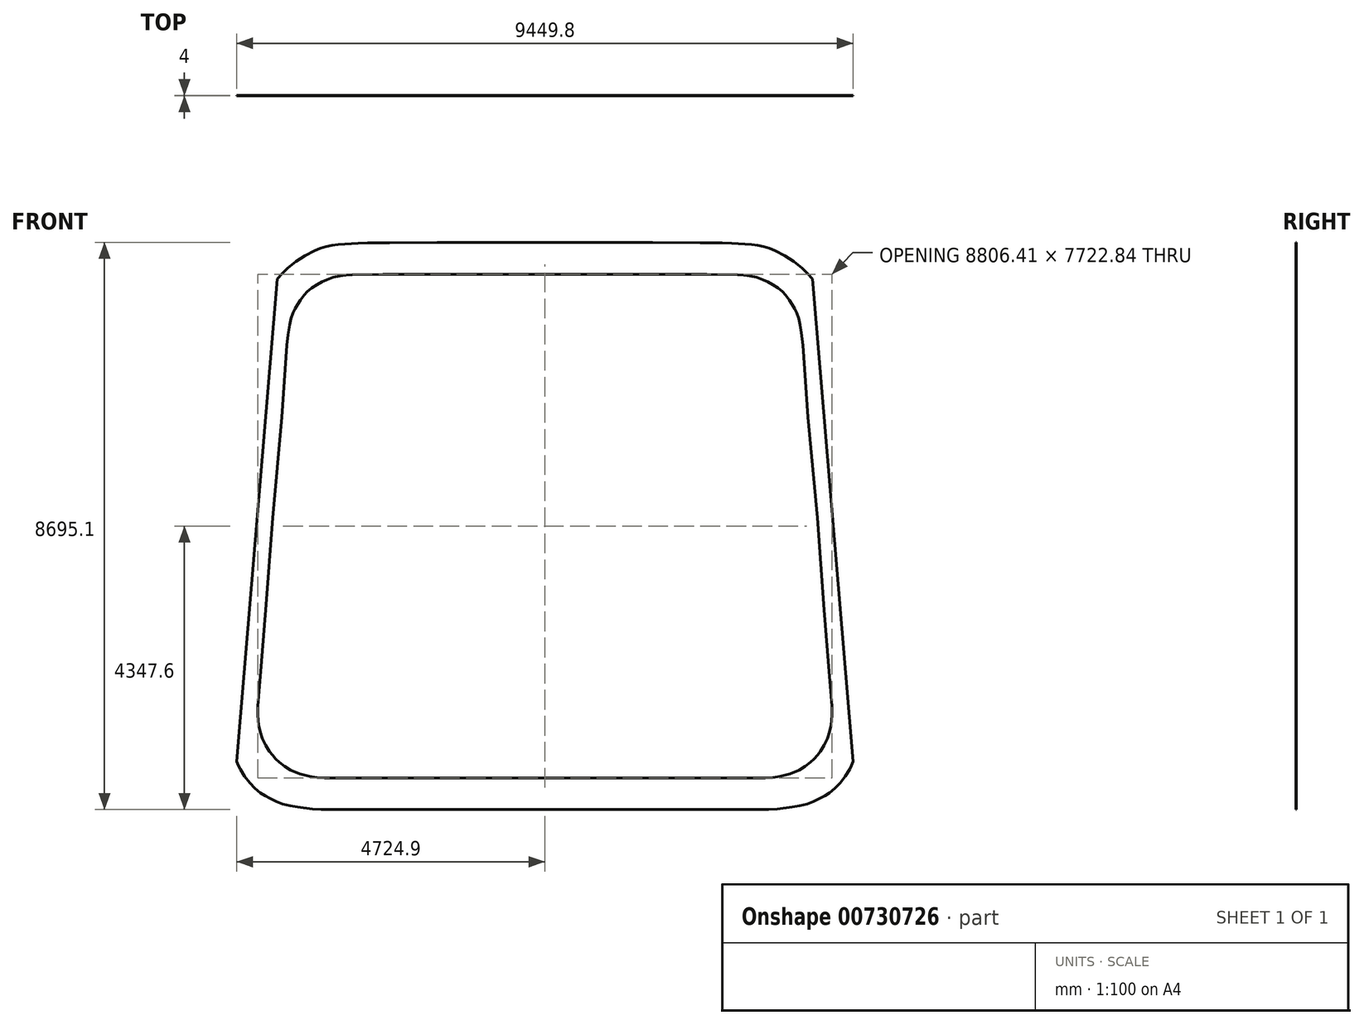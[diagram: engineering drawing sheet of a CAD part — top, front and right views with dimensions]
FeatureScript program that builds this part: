
annotation { "Feature Type Name" : "Feature", "Feature Type Description" : "" }
export const myFeature = defineFeature(function(context is Context, id is Id, definition is map)
    precondition{}
    {
        {
            var Q0;
            Q0=qCreatedBy(makeId("Front.planeOp"),FACE);
            var sketch = newSketch(context, id + "F0", { "sketchPlane" : qUnion([Q0])});
            skLineSegment(sketch, "E0", {"start": v(-4100.23, 3791.6) * mm, "end": v(-3973.7, 3780.9) * mm});
            skLineSegment(sketch, "E1", {"start": v(-3973.7, 3780.9) * mm, "end": v(-4100.23, 3791.6) * mm});
            skLineSegment(sketch, "E2", {"start": v(-4100.23, 3791.6) * mm, "end": v(-4023.75, 3874.4) * mm});
            skLineSegment(sketch, "E3", {"start": v(-4023.75, 3874.4) * mm, "end": v(-3941.84, 3951.8) * mm});
            skLineSegment(sketch, "E4", {"start": v(-3941.84, 3951.8) * mm, "end": v(-3814.61, 4053.62) * mm});
            skLineSegment(sketch, "E5", {"start": v(-3814.61, 4053.62) * mm, "end": v(-3675.57, 4146.44) * mm});
            skLineSegment(sketch, "E6", {"start": v(-3675.57, 4146.44) * mm, "end": v(-3530.84, 4221.57) * mm});
            skLineSegment(sketch, "E7", {"start": v(-3530.84, 4221.57) * mm, "end": v(-3443.72, 4257.71) * mm});
            skLineSegment(sketch, "E8", {"start": v(-3443.72, 4257.71) * mm, "end": v(-3354, 4285.83) * mm});
            skLineSegment(sketch, "E9", {"start": v(-3354, 4285.83) * mm, "end": v(-3261.07, 4304.07) * mm});
            skLineSegment(sketch, "E10", {"start": v(-3261.07, 4304.07) * mm, "end": v(-3166.73, 4315.7) * mm});
            skLineSegment(sketch, "E11", {"start": v(-3166.73, 4315.7) * mm, "end": v(-2864.57, 4338.46) * mm});
            skLineSegment(sketch, "E12", {"start": v(-2864.57, 4338.46) * mm, "end": v(-2717.79, 4342.65) * mm});
            skLineSegment(sketch, "E13", {"start": v(-2717.79, 4342.65) * mm, "end": v(-2714.16, 4215.7) * mm});
            skLineSegment(sketch, "E14", {"start": v(-2714.16, 4215.7) * mm, "end": v(-2717.79, 4342.65) * mm});
            skLineSegment(sketch, "E15", {"start": v(-2717.79, 4342.65) * mm, "end": v(-2379.79, 4343.31) * mm});
            skLineSegment(sketch, "E16", {"start": v(-2379.79, 4343.31) * mm, "end": v(-1650.99, 4346.03) * mm});
            skLineSegment(sketch, "E17", {"start": v(-1650.99, 4346.03) * mm, "end": v(-1312.13, 4347.55) * mm});
            skLineSegment(sketch, "E18", {"start": v(-1312.13, 4347.55) * mm, "end": v(-177.03, 4347.55) * mm});
            skLineSegment(sketch, "E19", {"start": v(-177.03, 4347.55) * mm, "end": v(-0.01, 4347.55) * mm});
            skLineSegment(sketch, "E20", {"start": v(-0.01, 4347.55) * mm, "end": v(-0.01, 4220.55) * mm});
            skLineSegment(sketch, "E21", {"start": v(-0.01, 4220.55) * mm, "end": v(-0.01, 4347.55) * mm});
            skLineSegment(sketch, "E22", {"start": v(-0.01, 4347.55) * mm, "end": v(177, 4347.55) * mm});
            skLineSegment(sketch, "E23", {"start": v(177, 4347.55) * mm, "end": v(1312.13, 4347.55) * mm});
            skLineSegment(sketch, "E24", {"start": v(1312.13, 4347.55) * mm, "end": v(1650.99, 4346.03) * mm});
            skLineSegment(sketch, "E25", {"start": v(1650.99, 4346.03) * mm, "end": v(2379.79, 4343.31) * mm});
            skLineSegment(sketch, "E26", {"start": v(2379.79, 4343.31) * mm, "end": v(2717.79, 4342.65) * mm});
            skLineSegment(sketch, "E27", {"start": v(2717.79, 4342.65) * mm, "end": v(2717.53, 4215.65) * mm});
            skLineSegment(sketch, "E28", {"start": v(2717.53, 4215.65) * mm, "end": v(2717.79, 4342.65) * mm});
            skLineSegment(sketch, "E29", {"start": v(2717.79, 4342.65) * mm, "end": v(2864.57, 4338.46) * mm});
            skLineSegment(sketch, "E30", {"start": v(2864.57, 4338.46) * mm, "end": v(3166.73, 4315.7) * mm});
            skLineSegment(sketch, "E31", {"start": v(3166.73, 4315.7) * mm, "end": v(3261.04, 4304.07) * mm});
            skLineSegment(sketch, "E32", {"start": v(3261.04, 4304.07) * mm, "end": v(3354, 4285.83) * mm});
            skLineSegment(sketch, "E33", {"start": v(3354, 4285.83) * mm, "end": v(3443.72, 4257.71) * mm});
            skLineSegment(sketch, "E34", {"start": v(3443.72, 4257.71) * mm, "end": v(3530.84, 4221.57) * mm});
            skLineSegment(sketch, "E35", {"start": v(3530.84, 4221.57) * mm, "end": v(3675.57, 4146.44) * mm});
            skLineSegment(sketch, "E36", {"start": v(3675.57, 4146.44) * mm, "end": v(3814.61, 4053.62) * mm});
            skLineSegment(sketch, "E37", {"start": v(3814.61, 4053.62) * mm, "end": v(3941.81, 3951.8) * mm});
            skLineSegment(sketch, "E38", {"start": v(3941.81, 3951.8) * mm, "end": v(4023.75, 3874.4) * mm});
            skLineSegment(sketch, "E39", {"start": v(4023.75, 3874.4) * mm, "end": v(4100.23, 3791.6) * mm});
            skLineSegment(sketch, "E40", {"start": v(4100.23, 3791.6) * mm, "end": v(4006.94, 3705.42) * mm});
            skLineSegment(sketch, "E41", {"start": v(4006.94, 3705.42) * mm, "end": v(4100.23, 3791.6) * mm});
            skLineSegment(sketch, "E42", {"start": v(4100.23, 3791.6) * mm, "end": v(4724.9, -3609.56) * mm});
            skLineSegment(sketch, "E43", {"start": v(4724.9, -3609.56) * mm, "end": v(4598.35, -3620.22) * mm});
            skLineSegment(sketch, "E44", {"start": v(4598.35, -3620.22) * mm, "end": v(4724.9, -3609.56) * mm});
            skLineSegment(sketch, "E45", {"start": v(4724.9, -3609.56) * mm, "end": v(4697.95, -3673.59) * mm});
            skLineSegment(sketch, "E46", {"start": v(4697.95, -3673.59) * mm, "end": v(4670.34, -3731.88) * mm});
            skLineSegment(sketch, "E47", {"start": v(4670.34, -3731.88) * mm, "end": v(4605.29, -3835.34) * mm});
            skLineSegment(sketch, "E48", {"start": v(4605.29, -3835.34) * mm, "end": v(4524.26, -3938.16) * mm});
            skLineSegment(sketch, "E49", {"start": v(4524.26, -3938.16) * mm, "end": v(4447.4, -4018.22) * mm});
            skLineSegment(sketch, "E50", {"start": v(4447.4, -4018.22) * mm, "end": v(4362, -4088.6) * mm});
            skLineSegment(sketch, "E51", {"start": v(4362, -4088.6) * mm, "end": v(4289.7, -4135) * mm});
            skLineSegment(sketch, "E52", {"start": v(4289.7, -4135) * mm, "end": v(4214.05, -4176.59) * mm});
            skLineSegment(sketch, "E53", {"start": v(4214.05, -4176.59) * mm, "end": v(4117.45, -4224.67) * mm});
            skLineSegment(sketch, "E54", {"start": v(4117.45, -4224.67) * mm, "end": v(4017.58, -4263.7) * mm});
            skLineSegment(sketch, "E55", {"start": v(4017.58, -4263.7) * mm, "end": v(3904.88, -4290.91) * mm});
            skLineSegment(sketch, "E56", {"start": v(3904.88, -4290.91) * mm, "end": v(3789.7, -4309.43) * mm});
            skLineSegment(sketch, "E57", {"start": v(3789.7, -4309.43) * mm, "end": v(3564.62, -4339.93) * mm});
            skLineSegment(sketch, "E58", {"start": v(3564.62, -4339.93) * mm, "end": v(3428.99, -4347.55) * mm});
            skLineSegment(sketch, "E59", {"start": v(3428.99, -4347.55) * mm, "end": v(3421.88, -4220.73) * mm});
            skLineSegment(sketch, "E60", {"start": v(3421.88, -4220.73) * mm, "end": v(3428.99, -4347.55) * mm});
            skLineSegment(sketch, "E61", {"start": v(3428.99, -4347.55) * mm, "end": v(3169.86, -4347.55) * mm});
            skLineSegment(sketch, "E62", {"start": v(3169.86, -4347.55) * mm, "end": v(2285.99, -4347.55) * mm});
            skLineSegment(sketch, "E63", {"start": v(2285.99, -4347.55) * mm, "end": v(2195.92, -4347.55) * mm});
            skLineSegment(sketch, "E64", {"start": v(2195.92, -4347.55) * mm, "end": v(1142.99, -4347.55) * mm});
            skLineSegment(sketch, "E65", {"start": v(1142.99, -4347.55) * mm, "end": v(1138.31, -4347.55) * mm});
            skLineSegment(sketch, "E66", {"start": v(1138.31, -4347.55) * mm, "end": v(-0.01, -4347.55) * mm});
            skLineSegment(sketch, "E67", {"start": v(-0.01, -4347.55) * mm, "end": v(-0.01, -4220.55) * mm});
            skLineSegment(sketch, "E68", {"start": v(-0.01, -4220.55) * mm, "end": v(-0.01, -4347.55) * mm});
            skLineSegment(sketch, "E69", {"start": v(-0.01, -4347.55) * mm, "end": v(-1138.31, -4347.55) * mm});
            skLineSegment(sketch, "E70", {"start": v(-1138.31, -4347.55) * mm, "end": v(-1143.01, -4347.55) * mm});
            skLineSegment(sketch, "E71", {"start": v(-1143.01, -4347.55) * mm, "end": v(-2195.92, -4347.55) * mm});
            skLineSegment(sketch, "E72", {"start": v(-2195.92, -4347.55) * mm, "end": v(-2286.01, -4347.55) * mm});
            skLineSegment(sketch, "E73", {"start": v(-2286.01, -4347.55) * mm, "end": v(-3169.86, -4347.55) * mm});
            skLineSegment(sketch, "E74", {"start": v(-3169.86, -4347.55) * mm, "end": v(-3429.01, -4347.55) * mm});
            skLineSegment(sketch, "E75", {"start": v(-3429.01, -4347.55) * mm, "end": v(-3429.01, -4220.55) * mm});
            skLineSegment(sketch, "E76", {"start": v(-3429.01, -4220.55) * mm, "end": v(-3429.01, -4347.55) * mm});
            skLineSegment(sketch, "E77", {"start": v(-3429.01, -4347.55) * mm, "end": v(-3564.62, -4339.93) * mm});
            skLineSegment(sketch, "E78", {"start": v(-3564.62, -4339.93) * mm, "end": v(-3789.7, -4309.43) * mm});
            skLineSegment(sketch, "E79", {"start": v(-3789.7, -4309.43) * mm, "end": v(-3904.88, -4290.91) * mm});
            skLineSegment(sketch, "E80", {"start": v(-3904.88, -4290.91) * mm, "end": v(-4017.58, -4263.7) * mm});
            skLineSegment(sketch, "E81", {"start": v(-4017.58, -4263.7) * mm, "end": v(-4117.45, -4224.67) * mm});
            skLineSegment(sketch, "E82", {"start": v(-4117.45, -4224.67) * mm, "end": v(-4214.05, -4176.59) * mm});
            skLineSegment(sketch, "E83", {"start": v(-4214.05, -4176.59) * mm, "end": v(-4289.7, -4135) * mm});
            skLineSegment(sketch, "E84", {"start": v(-4289.7, -4135) * mm, "end": v(-4362, -4088.6) * mm});
            skLineSegment(sketch, "E85", {"start": v(-4362, -4088.6) * mm, "end": v(-4447.4, -4018.22) * mm});
            skLineSegment(sketch, "E86", {"start": v(-4447.4, -4018.22) * mm, "end": v(-4524.26, -3938.16) * mm});
            skLineSegment(sketch, "E87", {"start": v(-4524.26, -3938.16) * mm, "end": v(-4605.29, -3835.34) * mm});
            skLineSegment(sketch, "E88", {"start": v(-4605.29, -3835.34) * mm, "end": v(-4670.34, -3731.88) * mm});
            skLineSegment(sketch, "E89", {"start": v(-4670.34, -3731.88) * mm, "end": v(-4697.95, -3673.59) * mm});
            skLineSegment(sketch, "E90", {"start": v(-4697.95, -3673.59) * mm, "end": v(-4724.9, -3609.56) * mm});
            skLineSegment(sketch, "E91", {"start": v(-4724.9, -3609.56) * mm, "end": v(-4607.85, -3560.28) * mm});
            skLineSegment(sketch, "E92", {"start": v(-4607.85, -3560.28) * mm, "end": v(-4724.9, -3609.56) * mm});
            skLineSegment(sketch, "E93", {"start": v(-4724.9, -3609.56) * mm, "end": v(-4100.23, 3791.6) * mm});
            skLineSegment(sketch, "E94", {"start": v(1492.57, 3861.47) * mm, "end": v(-0.01, 3861.47) * mm});
            skLineSegment(sketch, "E95", {"start": v(-0.01, 3861.47) * mm, "end": v(-0.01, 3988.47) * mm});
            skLineSegment(sketch, "E96", {"start": v(-0.01, 3988.47) * mm, "end": v(-0.01, 3861.47) * mm});
            skLineSegment(sketch, "E97", {"start": v(-0.01, 3861.47) * mm, "end": v(-1492.6, 3861.47) * mm});
            skLineSegment(sketch, "E98", {"start": v(-1492.6, 3861.47) * mm, "end": v(-2485.66, 3861.47) * mm});
            skLineSegment(sketch, "E99", {"start": v(-2485.66, 3861.47) * mm, "end": v(-2952.2, 3850.5) * mm});
            skLineSegment(sketch, "E100", {"start": v(-2952.2, 3850.5) * mm, "end": v(-2955.18, 3977.45) * mm});
            skLineSegment(sketch, "E101", {"start": v(-2955.18, 3977.45) * mm, "end": v(-2952.2, 3850.5) * mm});
            skLineSegment(sketch, "E102", {"start": v(-2952.2, 3850.5) * mm, "end": v(-3049.13, 3847.53) * mm});
            skLineSegment(sketch, "E103", {"start": v(-3049.13, 3847.53) * mm, "end": v(-3145.42, 3835.1) * mm});
            skLineSegment(sketch, "E104", {"start": v(-3145.42, 3835.1) * mm, "end": v(-3243.08, 3812.22) * mm});
            skLineSegment(sketch, "E105", {"start": v(-3243.08, 3812.22) * mm, "end": v(-3337.8, 3779.48) * mm});
            skLineSegment(sketch, "E106", {"start": v(-3337.8, 3779.48) * mm, "end": v(-3417.81, 3743.13) * mm});
            skLineSegment(sketch, "E107", {"start": v(-3417.81, 3743.13) * mm, "end": v(-3494.95, 3700.61) * mm});
            skLineSegment(sketch, "E108", {"start": v(-3494.95, 3700.61) * mm, "end": v(-3573.31, 3649.28) * mm});
            skLineSegment(sketch, "E109", {"start": v(-3573.31, 3649.28) * mm, "end": v(-3644.89, 3589.41) * mm});
            skLineSegment(sketch, "E110", {"start": v(-3644.89, 3589.41) * mm, "end": v(-3690.91, 3539.32) * mm});
            skLineSegment(sketch, "E111", {"start": v(-3690.91, 3539.32) * mm, "end": v(-3784.43, 3625.23) * mm});
            skLineSegment(sketch, "E112", {"start": v(-3784.43, 3625.23) * mm, "end": v(-3690.91, 3539.32) * mm});
            skLineSegment(sketch, "E113", {"start": v(-3690.91, 3539.32) * mm, "end": v(-3744.1, 3468.08) * mm});
            skLineSegment(sketch, "E114", {"start": v(-3744.1, 3468.08) * mm, "end": v(-3792.41, 3393.07) * mm});
            skLineSegment(sketch, "E115", {"start": v(-3792.41, 3393.07) * mm, "end": v(-3828.99, 3331.48) * mm});
            skLineSegment(sketch, "E116", {"start": v(-3828.99, 3331.48) * mm, "end": v(-3860.5, 3267.52) * mm});
            skLineSegment(sketch, "E117", {"start": v(-3860.5, 3267.52) * mm, "end": v(-3889.7, 3178.37) * mm});
            skLineSegment(sketch, "E118", {"start": v(-3889.7, 3178.37) * mm, "end": v(-3909.78, 3085.93) * mm});
            skLineSegment(sketch, "E119", {"start": v(-3909.78, 3085.93) * mm, "end": v(-3936.78, 2929.4) * mm});
            skLineSegment(sketch, "E120", {"start": v(-3936.78, 2929.4) * mm, "end": v(-3953.27, 2772.02) * mm});
            skLineSegment(sketch, "E121", {"start": v(-3953.27, 2772.02) * mm, "end": v(-4079.58, 2785.25) * mm});
            skLineSegment(sketch, "E122", {"start": v(-4079.58, 2785.25) * mm, "end": v(-3953.27, 2772.02) * mm});
            skLineSegment(sketch, "E123", {"start": v(-3953.27, 2772.02) * mm, "end": v(-4030.81, 1671.1) * mm});
            skLineSegment(sketch, "E124", {"start": v(-4030.81, 1671.1) * mm, "end": v(-4175.37, 128.05) * mm});
            skLineSegment(sketch, "E125", {"start": v(-4175.37, 128.05) * mm, "end": v(-4278.74, -1286.78) * mm});
            skLineSegment(sketch, "E126", {"start": v(-4278.74, -1286.78) * mm, "end": v(-4363.58, -2303.95) * mm});
            skLineSegment(sketch, "E127", {"start": v(-4363.58, -2303.95) * mm, "end": v(-4403.2, -2759.6) * mm});
            skLineSegment(sketch, "E128", {"start": v(-4403.2, -2759.6) * mm, "end": v(-4529.75, -2748.57) * mm});
            skLineSegment(sketch, "E129", {"start": v(-4529.75, -2748.57) * mm, "end": v(-4403.2, -2759.6) * mm});
            skLineSegment(sketch, "E130", {"start": v(-4403.2, -2759.6) * mm, "end": v(-4402.9, -2906.59) * mm});
            skLineSegment(sketch, "E131", {"start": v(-4402.9, -2906.59) * mm, "end": v(-4385.86, -3052.91) * mm});
            skLineSegment(sketch, "E132", {"start": v(-4385.86, -3052.91) * mm, "end": v(-4362.74, -3159.16) * mm});
            skLineSegment(sketch, "E133", {"start": v(-4362.74, -3159.16) * mm, "end": v(-4328.68, -3262.16) * mm});
            skLineSegment(sketch, "E134", {"start": v(-4328.68, -3262.16) * mm, "end": v(-4280.67, -3362.52) * mm});
            skLineSegment(sketch, "E135", {"start": v(-4280.67, -3362.52) * mm, "end": v(-4220.78, -3456.37) * mm});
            skLineSegment(sketch, "E136", {"start": v(-4220.78, -3456.37) * mm, "end": v(-4175.34, -3514.66) * mm});
            skLineSegment(sketch, "E137", {"start": v(-4175.34, -3514.66) * mm, "end": v(-4125.7, -3569.3) * mm});
            skLineSegment(sketch, "E138", {"start": v(-4125.7, -3569.3) * mm, "end": v(-4219.74, -3654.7) * mm});
            skLineSegment(sketch, "E139", {"start": v(-4219.74, -3654.7) * mm, "end": v(-4125.7, -3569.3) * mm});
            skLineSegment(sketch, "E140", {"start": v(-4125.7, -3569.3) * mm, "end": v(-4072.27, -3620.68) * mm});
            skLineSegment(sketch, "E141", {"start": v(-4072.27, -3620.68) * mm, "end": v(-3989.72, -3686.31) * mm});
            skLineSegment(sketch, "E142", {"start": v(-3989.72, -3686.31) * mm, "end": v(-3900.03, -3741.76) * mm});
            skLineSegment(sketch, "E143", {"start": v(-3900.03, -3741.76) * mm, "end": v(-3757.56, -3802.04) * mm});
            skLineSegment(sketch, "E144", {"start": v(-3757.56, -3802.04) * mm, "end": v(-3607.04, -3839.3) * mm});
            skLineSegment(sketch, "E145", {"start": v(-3607.04, -3839.3) * mm, "end": v(-3493.2, -3854.13) * mm});
            skLineSegment(sketch, "E146", {"start": v(-3493.2, -3854.13) * mm, "end": v(-3378.7, -3860.66) * mm});
            skLineSegment(sketch, "E147", {"start": v(-3378.7, -3860.66) * mm, "end": v(-3302.01, -3861.37) * mm});
            skLineSegment(sketch, "E148", {"start": v(-3302.01, -3861.37) * mm, "end": v(-3303.18, -3988.37) * mm});
            skLineSegment(sketch, "E149", {"start": v(-3303.18, -3988.37) * mm, "end": v(-3302.01, -3861.37) * mm});
            skLineSegment(sketch, "E150", {"start": v(-3302.01, -3861.37) * mm, "end": v(-2286.01, -3861.37) * mm});
            skLineSegment(sketch, "E151", {"start": v(-2286.01, -3861.37) * mm, "end": v(-762.01, -3861.37) * mm});
            skLineSegment(sketch, "E152", {"start": v(-762.01, -3861.37) * mm, "end": v(-0.01, -3861.37) * mm});
            skLineSegment(sketch, "E153", {"start": v(-0.01, -3861.37) * mm, "end": v(-0.01, -3988.37) * mm});
            skLineSegment(sketch, "E154", {"start": v(-0.01, -3988.37) * mm, "end": v(-0.01, -3861.37) * mm});
            skLineSegment(sketch, "E155", {"start": v(-0.01, -3861.37) * mm, "end": v(761.99, -3861.37) * mm});
            skLineSegment(sketch, "E156", {"start": v(761.99, -3861.37) * mm, "end": v(2285.99, -3861.37) * mm});
            skLineSegment(sketch, "E157", {"start": v(2285.99, -3861.37) * mm, "end": v(3301.99, -3861.37) * mm});
            skLineSegment(sketch, "E158", {"start": v(3301.99, -3861.37) * mm, "end": v(3301.99, -3988.37) * mm});
            skLineSegment(sketch, "E159", {"start": v(3301.99, -3988.37) * mm, "end": v(3301.99, -3861.37) * mm});
            skLineSegment(sketch, "E160", {"start": v(3301.99, -3861.37) * mm, "end": v(3378.7, -3860.66) * mm});
            skLineSegment(sketch, "E161", {"start": v(3378.7, -3860.66) * mm, "end": v(3493.2, -3854.13) * mm});
            skLineSegment(sketch, "E162", {"start": v(3493.2, -3854.13) * mm, "end": v(3607.04, -3839.3) * mm});
            skLineSegment(sketch, "E163", {"start": v(3607.04, -3839.3) * mm, "end": v(3757.56, -3802.04) * mm});
            skLineSegment(sketch, "E164", {"start": v(3757.56, -3802.04) * mm, "end": v(3900.03, -3741.76) * mm});
            skLineSegment(sketch, "E165", {"start": v(3900.03, -3741.76) * mm, "end": v(3989.72, -3686.31) * mm});
            skLineSegment(sketch, "E166", {"start": v(3989.72, -3686.31) * mm, "end": v(4072.24, -3620.68) * mm});
            skLineSegment(sketch, "E167", {"start": v(4072.24, -3620.68) * mm, "end": v(4125.7, -3569.3) * mm});
            skLineSegment(sketch, "E168", {"start": v(4125.7, -3569.3) * mm, "end": v(4213.72, -3660.86) * mm});
            skLineSegment(sketch, "E169", {"start": v(4213.72, -3660.86) * mm, "end": v(4125.7, -3569.3) * mm});
            skLineSegment(sketch, "E170", {"start": v(4125.7, -3569.3) * mm, "end": v(4175.34, -3514.66) * mm});
            skLineSegment(sketch, "E171", {"start": v(4175.34, -3514.66) * mm, "end": v(4220.78, -3456.37) * mm});
            skLineSegment(sketch, "E172", {"start": v(4220.78, -3456.37) * mm, "end": v(4280.67, -3362.52) * mm});
            skLineSegment(sketch, "E173", {"start": v(4280.67, -3362.52) * mm, "end": v(4328.68, -3262.16) * mm});
            skLineSegment(sketch, "E174", {"start": v(4328.68, -3262.16) * mm, "end": v(4362.74, -3159.16) * mm});
            skLineSegment(sketch, "E175", {"start": v(4362.74, -3159.16) * mm, "end": v(4385.86, -3052.91) * mm});
            skLineSegment(sketch, "E176", {"start": v(4385.86, -3052.91) * mm, "end": v(4402.9, -2906.59) * mm});
            skLineSegment(sketch, "E177", {"start": v(4402.9, -2906.59) * mm, "end": v(4403.2, -2759.6) * mm});
            skLineSegment(sketch, "E178", {"start": v(4403.2, -2759.6) * mm, "end": v(4530.2, -2759.85) * mm});
            skLineSegment(sketch, "E179", {"start": v(4530.2, -2759.85) * mm, "end": v(4403.2, -2759.6) * mm});
            skLineSegment(sketch, "E180", {"start": v(4403.2, -2759.6) * mm, "end": v(4363.58, -2303.95) * mm});
            skLineSegment(sketch, "E181", {"start": v(4363.58, -2303.95) * mm, "end": v(4278.74, -1286.78) * mm});
            skLineSegment(sketch, "E182", {"start": v(4278.74, -1286.78) * mm, "end": v(4175.37, 128.05) * mm});
            skLineSegment(sketch, "E183", {"start": v(4175.37, 128.05) * mm, "end": v(4030.81, 1671.1) * mm});
            skLineSegment(sketch, "E184", {"start": v(4030.81, 1671.1) * mm, "end": v(3953.27, 2772.02) * mm});
            skLineSegment(sketch, "E185", {"start": v(3953.27, 2772.02) * mm, "end": v(3931.73, 2962.72) * mm});
            skLineSegment(sketch, "E186", {"start": v(3931.73, 2962.72) * mm, "end": v(4057.92, 2976.97) * mm});
            skLineSegment(sketch, "E187", {"start": v(4057.92, 2976.97) * mm, "end": v(3931.73, 2962.72) * mm});
            skLineSegment(sketch, "E188", {"start": v(3931.73, 2962.72) * mm, "end": v(3909.78, 3085.93) * mm});
            skLineSegment(sketch, "E189", {"start": v(3909.78, 3085.93) * mm, "end": v(3889.67, 3178.29) * mm});
            skLineSegment(sketch, "E190", {"start": v(3889.67, 3178.29) * mm, "end": v(3860.5, 3267.52) * mm});
            skLineSegment(sketch, "E191", {"start": v(3860.5, 3267.52) * mm, "end": v(3828.99, 3331.48) * mm});
            skLineSegment(sketch, "E192", {"start": v(3828.99, 3331.48) * mm, "end": v(3792.41, 3393.07) * mm});
            skLineSegment(sketch, "E193", {"start": v(3792.41, 3393.07) * mm, "end": v(3744.1, 3468.08) * mm});
            skLineSegment(sketch, "E194", {"start": v(3744.1, 3468.08) * mm, "end": v(3690.91, 3539.32) * mm});
            skLineSegment(sketch, "E195", {"start": v(3690.91, 3539.32) * mm, "end": v(3792.66, 3615.3) * mm});
            skLineSegment(sketch, "E196", {"start": v(3792.66, 3615.3) * mm, "end": v(3690.91, 3539.32) * mm});
            skLineSegment(sketch, "E197", {"start": v(3690.91, 3539.32) * mm, "end": v(3644.89, 3589.41) * mm});
            skLineSegment(sketch, "E198", {"start": v(3644.89, 3589.41) * mm, "end": v(3573.31, 3649.28) * mm});
            skLineSegment(sketch, "E199", {"start": v(3573.31, 3649.28) * mm, "end": v(3494.93, 3700.61) * mm});
            skLineSegment(sketch, "E200", {"start": v(3494.93, 3700.61) * mm, "end": v(3417.79, 3743.13) * mm});
            skLineSegment(sketch, "E201", {"start": v(3417.79, 3743.13) * mm, "end": v(3337.8, 3779.48) * mm});
            skLineSegment(sketch, "E202", {"start": v(3337.8, 3779.48) * mm, "end": v(3243.08, 3812.22) * mm});
            skLineSegment(sketch, "E203", {"start": v(3243.08, 3812.22) * mm, "end": v(3145.42, 3835.1) * mm});
            skLineSegment(sketch, "E204", {"start": v(3145.42, 3835.1) * mm, "end": v(3049.13, 3847.53) * mm});
            skLineSegment(sketch, "E205", {"start": v(3049.13, 3847.53) * mm, "end": v(2952.2, 3850.5) * mm});
            skLineSegment(sketch, "E206", {"start": v(2952.2, 3850.5) * mm, "end": v(2956.06, 3977.42) * mm});
            skLineSegment(sketch, "E207", {"start": v(2956.06, 3977.42) * mm, "end": v(2952.2, 3850.5) * mm});
            skLineSegment(sketch, "E208", {"start": v(2952.2, 3850.5) * mm, "end": v(2485.66, 3861.47) * mm});
            skLineSegment(sketch, "E209", {"start": v(2485.66, 3861.47) * mm, "end": v(1492.57, 3861.47) * mm});
            skSolve(sketch);
        }
        {
            var Q0;
            Q0 = qSketchRegion(id + "F0", true);
            extrude(context, id + "F1", {"entities" : qUnion([Q0]), "depth" : 4 * mm, "offsetDistance" : 25 * mm});
        }
    });
